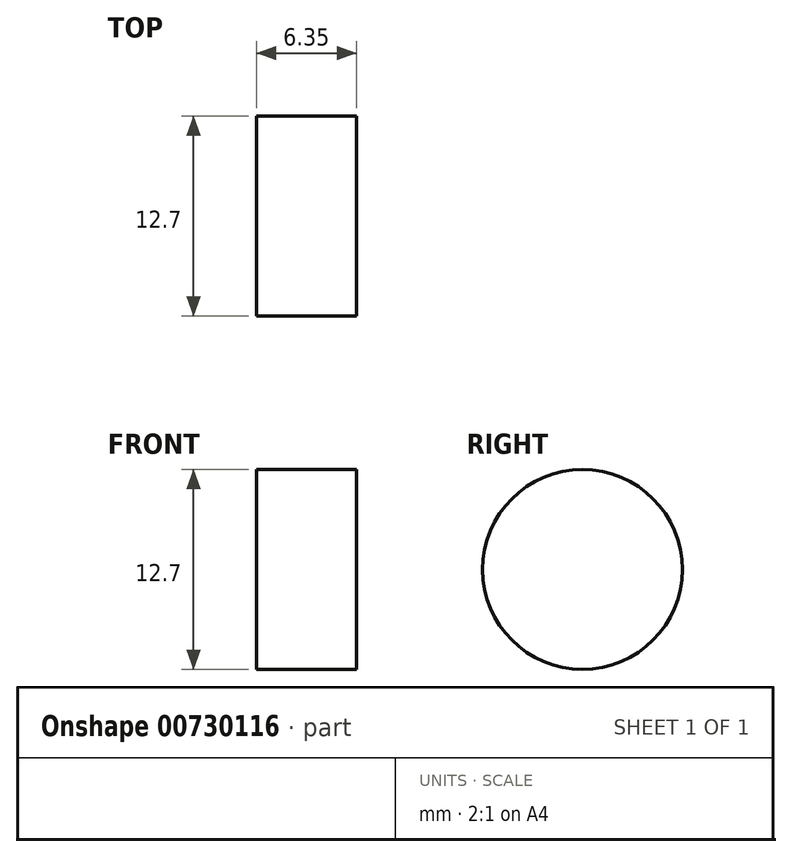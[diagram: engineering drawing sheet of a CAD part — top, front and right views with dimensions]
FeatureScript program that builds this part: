
annotation { "Feature Type Name" : "Feature", "Feature Type Description" : "" }
export const myFeature = defineFeature(function(context is Context, id is Id, definition is map)
    precondition{}
    {
        {
            var Q0;
            Q0=qCreatedBy(makeId("Front.planeOp"),FACE);
            var sketch = newSketch(context, id + "F0", { "sketchPlane" : qUnion([Q0])});
            skLineSegment(sketch, "E0", {"start": v(0, 0) * mm, "end": v(0, 6.35) * mm});
            skLineSegment(sketch, "E1", {"start": v(0, 6.35) * mm, "end": v(6.35, 6.35) * mm});
            skLineSegment(sketch, "E2", {"start": v(6.35, 6.35) * mm, "end": v(6.35, 0) * mm});
            skLineSegment(sketch, "E3", {"start": v(6.35, 0) * mm, "end": v(0, 0) * mm});
            skSolve(sketch);
        }
        {
            var Q0;
            Q0 = qSketchRegion(id + "F0", true);
            var Q1;
            Q1=sQuery(id+"F0.wireOp",EDGE,"E3");
            revolve(context, id + "F1", {"surfaceOperationType" : NewSurfaceOperationType.NEW, "entities" : qUnion([Q0]), "axis" : qUnion([Q1]), "revolveType" : RevolveType.FULL});
        }
    });
